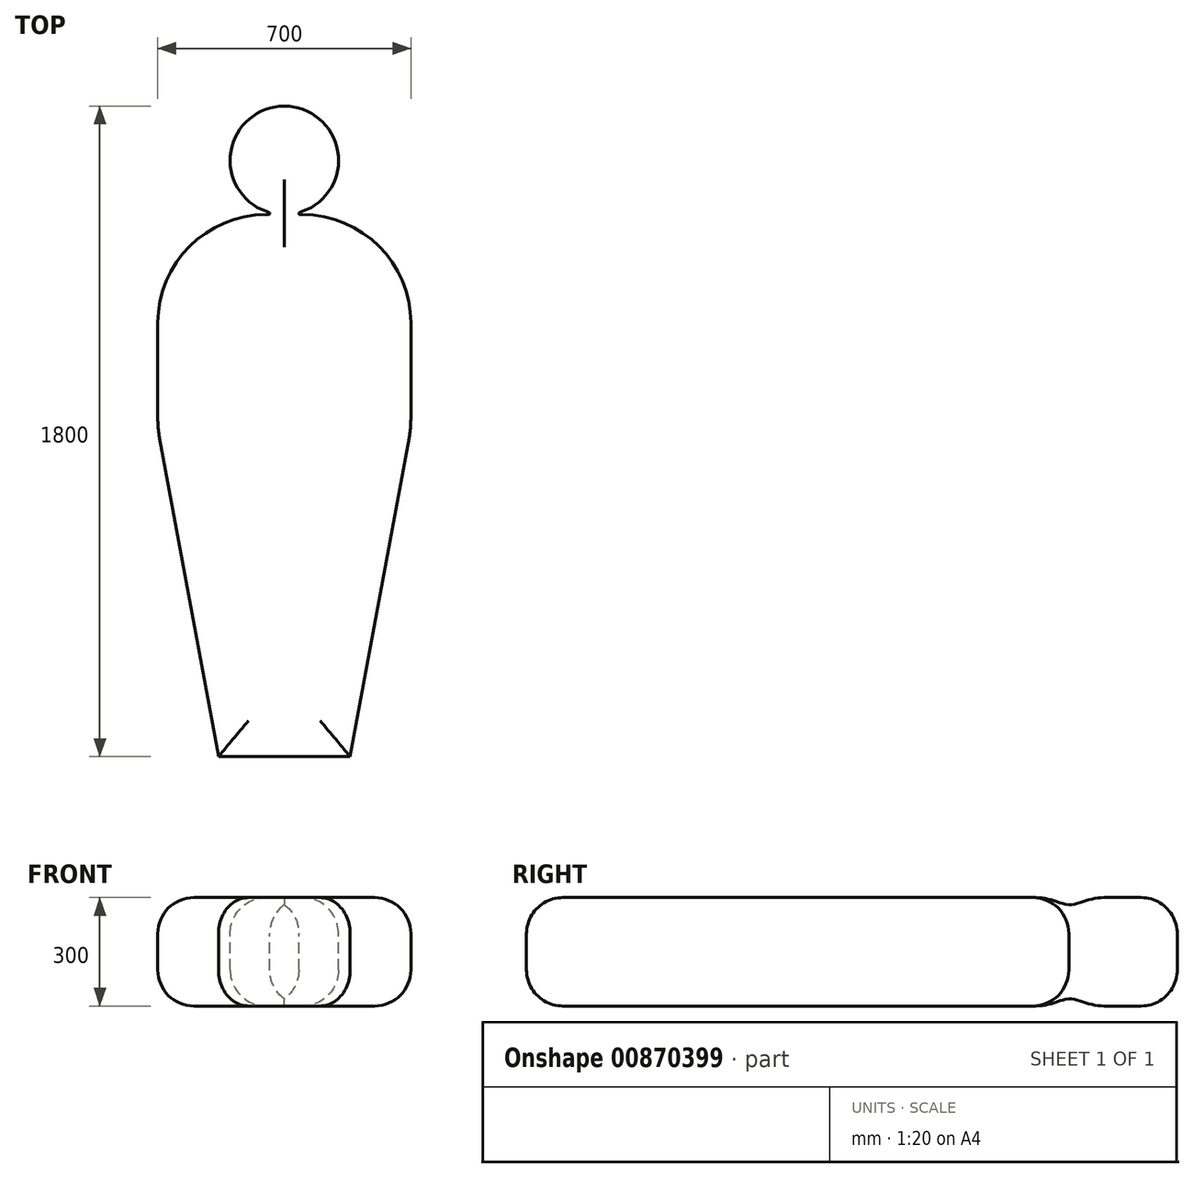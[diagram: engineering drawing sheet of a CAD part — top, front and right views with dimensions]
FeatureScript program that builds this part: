
annotation { "Feature Type Name" : "Feature", "Feature Type Description" : "" }
export const myFeature = defineFeature(function(context is Context, id is Id, definition is map)
    precondition{}
    {
        {
            var Q0;
            Q0=qCreatedBy(makeId("Top.planeOp"),FACE);
            var sketch = newSketch(context, id + "F0", { "sketchPlane" : qUnion([Q0])});
            skLineSegment(sketch, "E0", {"start": v(0, 0) * mm, "end": v(182.03, 0) * mm});
            skLineSegment(sketch, "E1", {"start": v(182.03, 0) * mm, "end": v(350, 908.5) * mm});
            skLineSegment(sketch, "E2", {"start": v(350, 908.5) * mm, "end": v(350, 1500) * mm});
            skLineSegment(sketch, "E3", {"start": v(350, 1500) * mm, "end": v(-350, 1500) * mm});
            skLineSegment(sketch, "E4", {"start": v(-350, 1500) * mm, "end": v(-350, 908.5) * mm});
            skLineSegment(sketch, "E5", {"start": v(-350, 908.5) * mm, "end": v(-182.03, 0) * mm});
            skLineSegment(sketch, "E6", {"start": v(-182.03, 0) * mm, "end": v(0, 0) * mm});
            skSolve(sketch);
        }
        {
            var Q0;
            Q0=makeQuery(id+"F0.imprint","IMPRINT",FACE,{"disambiguationData":[TD([[makeQuery(id+"F0.imprint","IMPRINT",EDGE,{"derivedFrom":sQuery(id+"F0.wireOp",EDGE,"E0")}),1.0]])]});
            extrude(context, id + "F1", {"entities" : qUnion([Q0]), "depth" : 300 * mm, "offsetDistance" : 25 * mm});
        }
        {
            var Q0;
            Q0=makeQuery(id+"F1.opExtrude","SWEPT_EDGE",EDGE,{"disambiguationData":[OSD([sQuery(id+"F0.wireOp",EDGE,"E2"),sQuery(id+"F0.wireOp",EDGE,"E3")])]});
            var Q1;
            Q1=makeQuery(id+"F1.opExtrude","SWEPT_EDGE",EDGE,{"disambiguationData":[OSD([sQuery(id+"F0.wireOp",EDGE,"E3"),sQuery(id+"F0.wireOp",EDGE,"E4")])]});
            var Q2;
            Q2=makeQuery(id+"F1.opExtrude","SWEPT_EDGE",EDGE,{"disambiguationData":[OSD([sQuery(id+"F0.wireOp",EDGE,"E4"),sQuery(id+"F0.wireOp",EDGE,"E5")])]});
            var Q3;
            Q3=makeQuery(id+"F1.opExtrude","SWEPT_EDGE",EDGE,{"disambiguationData":[OSD([sQuery(id+"F0.wireOp",EDGE,"E1"),sQuery(id+"F0.wireOp",EDGE,"E2")])]});
            fillet(context, id + "F2", {"entities" : qUnion([Q0, Q1, Q2, Q3]), "tangentPropagation" : true, "radius" : 300 * mm, "defaultsChanged" : false, "vertexSettings" : [], "allowEdgeOverflow" : false});
        }
        {
            var Q0;
            Q0=makeQuery(id+"F1.opExtrude","CAP_FACE",FACE,{"disambiguationData":[OSD([sQuery(id+"F0.wireOp",EDGE,"E0"),sQuery(id+"F0.wireOp",EDGE,"E1"),sQuery(id+"F0.wireOp",EDGE,"E2"),sQuery(id+"F0.wireOp",EDGE,"E3"),sQuery(id+"F0.wireOp",EDGE,"E4"),sQuery(id+"F0.wireOp",EDGE,"E5"),sQuery(id+"F0.wireOp",EDGE,"E6")])],"isStart":false});
            var sketch = newSketch(context, id + "F3", { "sketchPlane" : qUnion([Q0])});
            skCircle(sketch, "E7", {"center": v(0, 1650) * mm, "radius": 150 * mm});
            skLineSegment(sketch, "E8", {"start": v(50, 1500) * mm, "end": v(43.22, 1500) * mm});
            skLineSegment(sketch, "E9", {"start": v(42.22, 1505.83) * mm, "end": v(50, 1508.58) * mm});
            skPoint(sketch, "E10.newPointB", {"position": v(-50, 1500) * mm});
            skArc(sketch, "E10.filletArc", {"start": v(42.22, 1505.83) * mm, "mid": v(40.26, 1502.5) * mm, "end": v(43.22, 1500) * mm});
            skLineSegment(sketch, "E11", {"start": v(-50, 1500) * mm, "end": v(-43.22, 1500) * mm});
            skLineSegment(sketch, "E12", {"start": v(-42.22, 1505.83) * mm, "end": v(-50, 1508.58) * mm});
            skPoint(sketch, "E13.visualSharp", {"position": v(-25.74, 1500) * mm});
            skArc(sketch, "E13.filletArc", {"start": v(-43.22, 1500) * mm, "mid": v(-40.26, 1502.5) * mm, "end": v(-42.22, 1505.83) * mm});
            skSolve(sketch);
        }
        {
            var Q0;
            Q0 = qSketchRegion(id + "F3", true);
            var Q1;
            {var subQ0=sQuery(id+"F3.wireOp",EDGE,"E9");Q1=makeQuery(id+"F3.imprint","IMPRINT",FACE,{"disambiguationData":[TD([[makeQuery(id+"F3.imprint","IMPRINT",EDGE,{"derivedFrom":subQ0}),1.0]])]});}
            var Q2;
            {var subQ0=sQuery(id+"F3.wireOp",EDGE,"E12");Q2=makeQuery(id+"F3.imprint","IMPRINT",FACE,{"disambiguationData":[TD([[makeQuery(id+"F3.imprint","IMPRINT",EDGE,{"derivedFrom":subQ0}),-1.0]])]});}
            var Q3;
            Q3=makeQuery(id+"F1.opExtrude","CAP_FACE",FACE,{"disambiguationData":[OSD([sQuery(id+"F0.wireOp",EDGE,"E0"),sQuery(id+"F0.wireOp",EDGE,"E1"),sQuery(id+"F0.wireOp",EDGE,"E2"),sQuery(id+"F0.wireOp",EDGE,"E3"),sQuery(id+"F0.wireOp",EDGE,"E4"),sQuery(id+"F0.wireOp",EDGE,"E5"),sQuery(id+"F0.wireOp",EDGE,"E6")])],"isStart":true});
            extrude(context, id + "F4", {"entities" : qUnion([Q0, Q1, Q2]), "operationType" : NewBodyOperationType.ADD, "endBound" : BoundingType.UP_TO_SURFACE, "oppositeDirection" : true, "depth" : 25 * mm, "endBoundEntityFace" : qUnion([Q3]), "offsetDistance" : 25 * mm});
        }
        {
            var Q0;
            {var subQ0=sQuery(id+"F0.wireOp",EDGE,"E3");Q0=makeQuery(id+"F4.boolean.opBoolean","MERGE",FACE,{"derivedFrom":[makeQuery(id+"F1.opExtrude","CAP_FACE",FACE,{"disambiguationData":[OSD([sQuery(id+"F0.wireOp",EDGE,"E0"),sQuery(id+"F0.wireOp",EDGE,"E1"),sQuery(id+"F0.wireOp",EDGE,"E2"),subQ0,sQuery(id+"F0.wireOp",EDGE,"E4"),sQuery(id+"F0.wireOp",EDGE,"E5"),sQuery(id+"F0.wireOp",EDGE,"E6")])],"isStart":true}),makeQuery(id+"F4.opExtrude","CAP_FACE",FACE,{"disambiguationData":[OSD([subQ0,sQuery(id+"F3.wireOp",EDGE,"E7"),sQuery(id+"F3.wireOp",EDGE,"E9"),sQuery(id+"F3.wireOp",EDGE,"E10.filletArc"),sQuery(id+"F3.wireOp",EDGE,"E12"),sQuery(id+"F3.wireOp",EDGE,"E13.filletArc")])],"isStart":false})]});}
            var Q1;
            {var subQ0=sQuery(id+"F0.wireOp",EDGE,"E3");Q1=makeQuery(id+"F4.boolean.opBoolean","MERGE",FACE,{"derivedFrom":[makeQuery(id+"F1.opExtrude","CAP_FACE",FACE,{"disambiguationData":[OSD([sQuery(id+"F0.wireOp",EDGE,"E0"),sQuery(id+"F0.wireOp",EDGE,"E1"),sQuery(id+"F0.wireOp",EDGE,"E2"),subQ0,sQuery(id+"F0.wireOp",EDGE,"E4"),sQuery(id+"F0.wireOp",EDGE,"E5"),sQuery(id+"F0.wireOp",EDGE,"E6")])],"isStart":false}),makeQuery(id+"F4.opExtrude","CAP_FACE",FACE,{"disambiguationData":[OSD([subQ0,sQuery(id+"F3.wireOp",EDGE,"E7"),sQuery(id+"F3.wireOp",EDGE,"E9"),sQuery(id+"F3.wireOp",EDGE,"E10.filletArc"),sQuery(id+"F3.wireOp",EDGE,"E12"),sQuery(id+"F3.wireOp",EDGE,"E13.filletArc")])],"isStart":true})]});}
            fillet(context, id + "F5", {"entities" : qUnion([Q0, Q1]), "tangentPropagation" : true, "radius" : 100 * mm, "defaultsChanged" : false, "vertexSettings" : [], "allowEdgeOverflow" : false});
        }
    });
